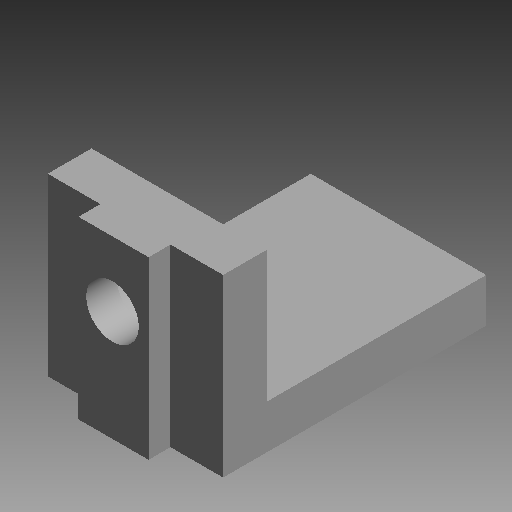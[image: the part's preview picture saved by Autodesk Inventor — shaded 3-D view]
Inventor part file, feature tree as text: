
AUTODESK INVENTOR PART (.ipt)
format: ipt  version: 2019 (Build 230136000, 136)  size: 92,672 bytes
history: native  units: mm (DEFAULTED — no unit token found)
features: other x3, sketch x3
ambient origin geometry x8: Origin, YZ Plane, XZ Plane, XY Plane, X Axis, Y Axis, Z Axis, Center Point
bodies: Solid1 (feature_tree)
feature tree (6):
  other  "spring tab for on arm"
  other  "Solid1::spring tab for on arm"
  other  "TaggingFeature1"
  sketch  "Sketch1"  dims[d0=10.0mm]
  sketch  "Sketch4"
  sketch  "Sketch5"
